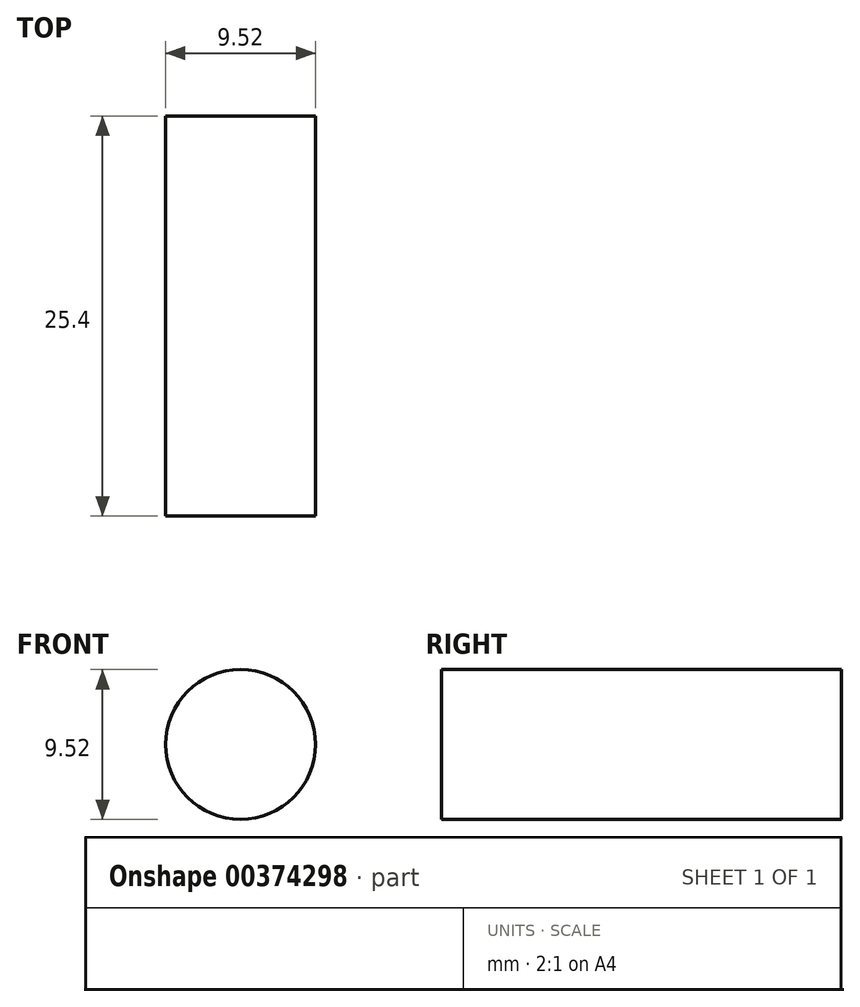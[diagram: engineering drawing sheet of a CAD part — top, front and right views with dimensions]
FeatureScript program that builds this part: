
annotation { "Feature Type Name" : "Feature", "Feature Type Description" : "" }
export const myFeature = defineFeature(function(context is Context, id is Id, definition is map)
    precondition{}
    {
        {
            var Q0;
            Q0=qCreatedBy(makeId("Front.planeOp"),FACE);
            var sketch = newSketch(context, id + "F0", { "sketchPlane" : qUnion([Q0])});
            skCircle(sketch, "E0", {"center": v(0, 0) * mm, "radius": 4.76 * mm});
            skSolve(sketch);
        }
        {
            var Q0;
            Q0 = qSketchRegion(id + "F0", true);
            extrude(context, id + "F1", {"entities" : qUnion([Q0]), "depth" : 25.4 * mm});
        }
    });
